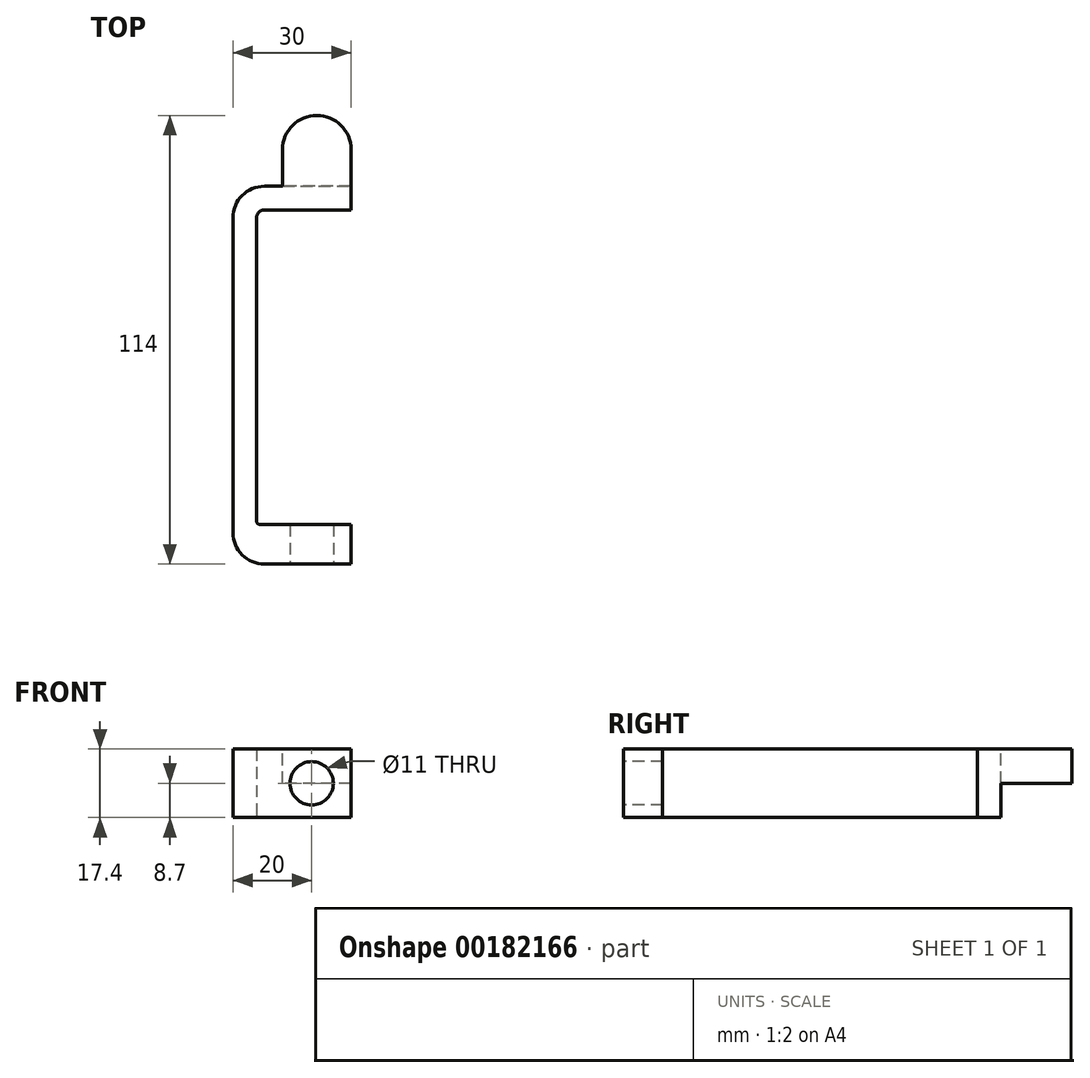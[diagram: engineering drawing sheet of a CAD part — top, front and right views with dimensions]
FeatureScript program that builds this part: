
annotation { "Feature Type Name" : "Feature", "Feature Type Description" : "" }
export const myFeature = defineFeature(function(context is Context, id is Id, definition is map)
    precondition{}
    {
        {
            var Q0;
            Q0=qCreatedBy(makeId("Top.planeOp"),FACE);
            var sketch = newSketch(context, id + "F0", { "sketchPlane" : qUnion([Q0])});
            skLineSegment(sketch, "E0.bottom", {"start": v(3, 47) * mm, "end": v(-3, 47) * mm});
            skLineSegment(sketch, "E0.top", {"start": v(3, -49) * mm, "end": v(-3, -49) * mm});
            skLineSegment(sketch, "E0.left", {"start": v(3, 47) * mm, "end": v(3, -49) * mm});
            skLineSegment(sketch, "E0.right", {"start": v(-3, 47) * mm, "end": v(-3, -49) * mm});
            skPoint(sketch, "E0.middle", {"position": v(0, -1) * mm});
            skLineSegment(sketch, "E1.bottom", {"start": v(3, 47) * mm, "end": v(27, 47) * mm});
            skLineSegment(sketch, "E1.top", {"start": v(3, 41) * mm, "end": v(27, 41) * mm});
            skLineSegment(sketch, "E1.left", {"start": v(3, 47) * mm, "end": v(3, 41) * mm});
            skLineSegment(sketch, "E1.right", {"start": v(27, 47) * mm, "end": v(27, 41) * mm});
            skLineSegment(sketch, "E2.bottom", {"start": v(3, -49) * mm, "end": v(27, -49) * mm});
            skLineSegment(sketch, "E2.top", {"start": v(3, -39) * mm, "end": v(27, -39) * mm});
            skLineSegment(sketch, "E2.left", {"start": v(3, -49) * mm, "end": v(3, -39) * mm});
            skLineSegment(sketch, "E2.right", {"start": v(27, -49) * mm, "end": v(27, -39) * mm});
            skSolve(sketch);
        }
        {
            var Q0;
            Q0 = qSketchRegion(id + "F0", true);
            extrude(context, id + "F1", {"entities" : qUnion([Q0]), "depth" : 17.4 * mm});
        }
        {
            var Q0;
            Q0=makeQuery(id+"F1.opExtrude","SWEPT_EDGE",EDGE,{"disambiguationData":[OSD([sQuery(id+"F0.wireOp",EDGE,"E0.bottom"),sQuery(id+"F0.wireOp",EDGE,"E0.right")])]});
            var Q1;
            Q1=makeQuery(id+"F1.opExtrude","SWEPT_EDGE",EDGE,{"disambiguationData":[OSD([sQuery(id+"F0.wireOp",EDGE,"E0.top"),sQuery(id+"F0.wireOp",EDGE,"E0.right")])]});
            fillet(context, id + "F2", {"entities" : qUnion([Q0, Q1]), "radius" : 8 * mm, "tangentPropagation" : true, "allowEdgeOverflow" : false});
        }
        {
            var Q0;
            Q0=makeQuery(id+"F1.opExtrude","SWEPT_EDGE",EDGE,{"disambiguationData":[OSD([sQuery(id+"F0.wireOp",EDGE,"E0.left"),sQuery(id+"F0.wireOp",EDGE,"E1.top"),sQuery(id+"F0.wireOp",EDGE,"E1.left")])]});
            fillet(context, id + "F3", {"entities" : qUnion([Q0]), "radius" : 2 * mm, "tangentPropagation" : true, "allowEdgeOverflow" : false});
        }
        {
            var Q0;
            Q0=makeQuery(id+"F1.opExtrude","SWEPT_FACE",FACE,{"disambiguationData":[OSD([sQuery(id+"F0.wireOp",EDGE,"E0.bottom"),sQuery(id+"F0.wireOp",EDGE,"E1.bottom")])]});
            var sketch = newSketch(context, id + "F4", { "sketchPlane" : qUnion([Q0])});
            skLineSegment(sketch, "E3", {"start": v(-27, 8.7) * mm, "end": v(-9.6, 8.7) * mm});
            skLineSegment(sketch, "E4", {"start": v(-9.6, 8.7) * mm, "end": v(-9.6, 17.4) * mm});
            skLineSegment(sketch, "E5", {"start": v(-9.6, 17.4) * mm, "end": v(-27, 17.4) * mm});
            skLineSegment(sketch, "E6", {"start": v(-27, 17.4) * mm, "end": v(-27, 8.7) * mm});
            skSolve(sketch);
        }
        {
            var Q0;
            Q0=makeQuery(id+"F1.opExtrude","SWEPT_FACE",FACE,{"disambiguationData":[OSD([sQuery(id+"F0.wireOp",EDGE,"E0.top"),sQuery(id+"F0.wireOp",EDGE,"E2.bottom")])]});
            var sketch = newSketch(context, id + "F5", { "sketchPlane" : qUnion([Q0])});
            skCircle(sketch, "E7", {"center": v(17, 8.7) * mm, "radius": 5.5 * mm});
            skPoint(sketch, "E7.centerSnap0", {"position": v(27, 8.7) * mm});
            skSolve(sketch);
        }
        {
            var Q0;
            Q0 = qSketchRegion(id + "F5", true);
            extrude(context, id + "F6", {"entities" : qUnion([Q0]), "operationType" : NewBodyOperationType.REMOVE, "oppositeDirection" : true, "depth" : 25 * mm});
        }
        {
            var Q0;
            Q0=makeQuery(id+"F1.opExtrude","SWEPT_EDGE",EDGE,{"disambiguationData":[OSD([sQuery(id+"F0.wireOp",EDGE,"E0.left"),sQuery(id+"F0.wireOp",EDGE,"E2.top"),sQuery(id+"F0.wireOp",EDGE,"E2.left")])]});
            fillet(context, id + "F7", {"entities" : qUnion([Q0]), "radius" : 1 * mm, "tangentPropagation" : true, "allowEdgeOverflow" : false});
        }
        {
            var Q0;
            Q0=makeQuery(id+"F4.imprint","IMPRINT",FACE,{"disambiguationData":[TD([[makeQuery(id+"F4.imprint","IMPRINT",EDGE,{"derivedFrom":sQuery(id+"F4.wireOp",EDGE,"E3")}),1.0]])]});
            extrude(context, id + "F8", {"entities" : qUnion([Q0]), "operationType" : NewBodyOperationType.ADD, "depth" : 18 * mm});
        }
        {
            var Q0;
            Q0=makeQuery(id+"F8.opExtrude","CAP_EDGE",EDGE,{"disambiguationData":[OSD([sQuery(id+"F4.wireOp",EDGE,"E6")])],"isStart":false});
            var Q1;
            Q1=makeQuery(id+"F8.opExtrude","CAP_EDGE",EDGE,{"disambiguationData":[OSD([sQuery(id+"F4.wireOp",EDGE,"E4")])],"isStart":false});
            fillet(context, id + "F9", {"entities" : qUnion([Q0, Q1]), "radius" : 8.7 * mm, "tangentPropagation" : true, "allowEdgeOverflow" : false});
        }
    });
